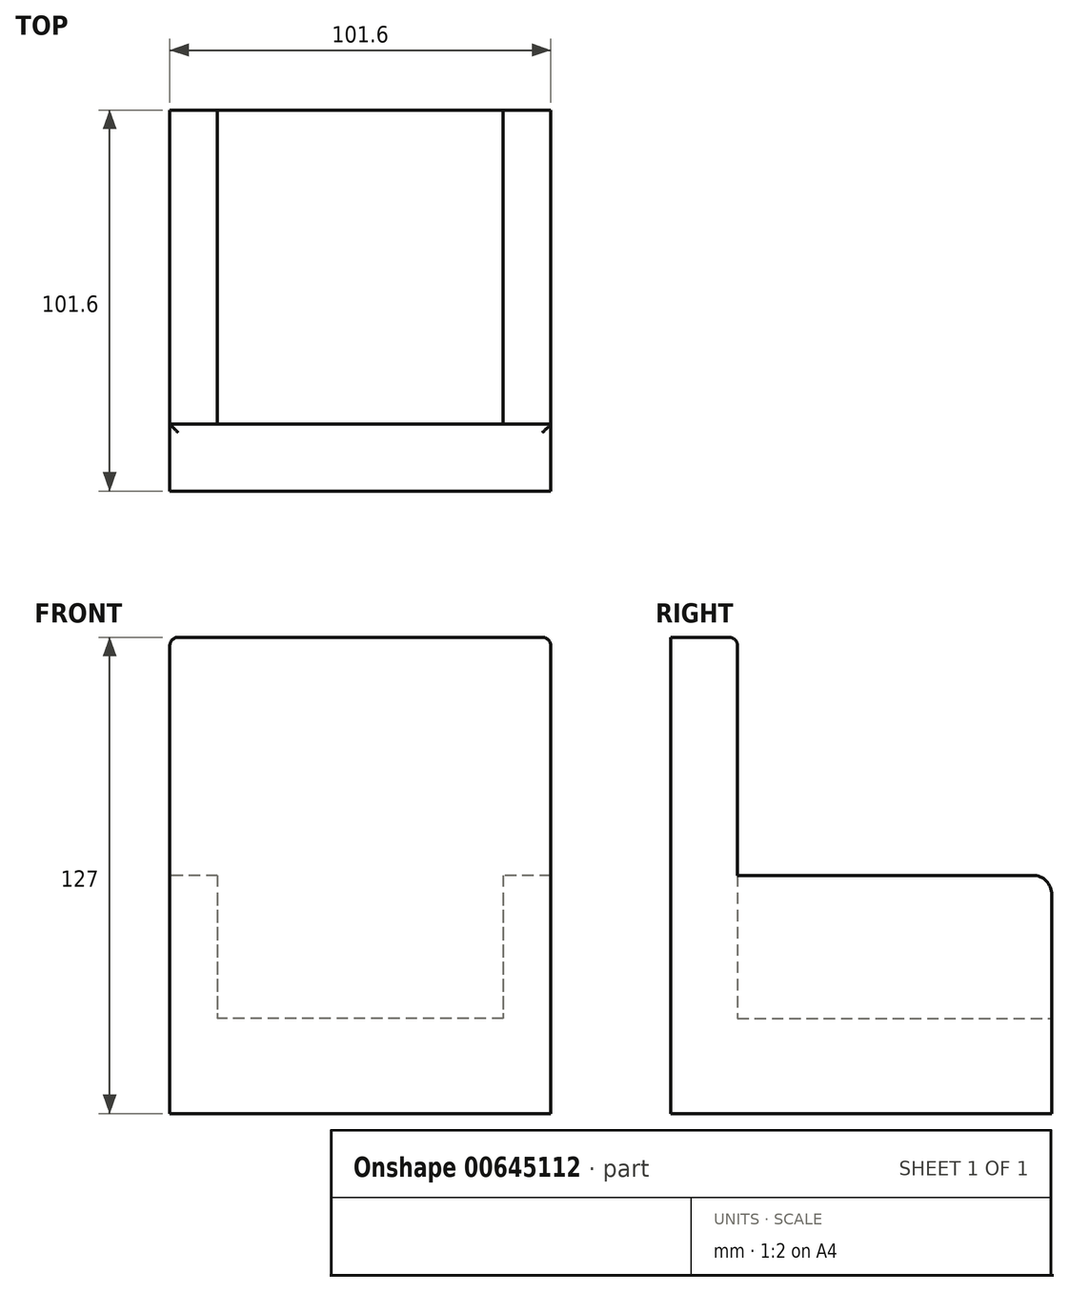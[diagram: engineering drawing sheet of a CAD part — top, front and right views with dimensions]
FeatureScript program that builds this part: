
annotation { "Feature Type Name" : "Feature", "Feature Type Description" : "" }
export const myFeature = defineFeature(function(context is Context, id is Id, definition is map)
    precondition{}
    {
        {
            var Q0;
            Q0=qCreatedBy(makeId("Top.planeOp"),FACE);
            var sketch = newSketch(context, id + "F0", { "sketchPlane" : qUnion([Q0])});
            skLineSegment(sketch, "E0.bottom", {"start": v(-50.64, 54.03) * mm, "end": v(50.96, 54.03) * mm});
            skLineSegment(sketch, "E0.top", {"start": v(-50.64, -47.57) * mm, "end": v(50.96, -47.57) * mm});
            skLineSegment(sketch, "E0.left", {"start": v(-50.64, 54.03) * mm, "end": v(-50.64, -47.57) * mm});
            skLineSegment(sketch, "E0.right", {"start": v(50.96, 54.03) * mm, "end": v(50.96, -47.57) * mm});
            skSolve(sketch);
        }
        {
            var Q0;
            Q0 = qSketchRegion(id + "F0", true);
            extrude(context, id + "F1", {"entities" : qUnion([Q0]), "depth" : 25.4 * mm, "offsetDistance" : 25.4 * mm});
        }
        {
            var Q0;
            Q0=makeQuery(id+"F1.opExtrude","CAP_FACE",FACE,{"disambiguationData":[OSD([sQuery(id+"F0.wireOp",EDGE,"E0.bottom"),sQuery(id+"F0.wireOp",EDGE,"E0.top"),sQuery(id+"F0.wireOp",EDGE,"E0.left"),sQuery(id+"F0.wireOp",EDGE,"E0.right")])],"isStart":false});
            var sketch = newSketch(context, id + "F2", { "sketchPlane" : qUnion([Q0])});
            skLineSegment(sketch, "E1.bottom", {"start": v(50.96, -47.57) * mm, "end": v(-50.64, -47.57) * mm});
            skLineSegment(sketch, "E1.top", {"start": v(50.96, -29.78) * mm, "end": v(-50.64, -29.78) * mm});
            skLineSegment(sketch, "E1.left", {"start": v(50.96, -47.57) * mm, "end": v(50.96, -29.78) * mm});
            skLineSegment(sketch, "E1.right", {"start": v(-50.64, -47.57) * mm, "end": v(-50.64, -29.78) * mm});
            skSolve(sketch);
        }
        {
            var Q0;
            Q0 = qSketchRegion(id + "F2", true);
            extrude(context, id + "F3", {"entities" : qUnion([Q0]), "operationType" : NewBodyOperationType.ADD, "depth" : 101.6 * mm, "offsetDistance" : 25.4 * mm});
        }
        {
            var Q0;
            Q0=makeQuery(id+"F1.opExtrude","CAP_FACE",FACE,{"disambiguationData":[OSD([sQuery(id+"F0.wireOp",EDGE,"E0.bottom"),sQuery(id+"F0.wireOp",EDGE,"E0.top"),sQuery(id+"F0.wireOp",EDGE,"E0.left"),sQuery(id+"F0.wireOp",EDGE,"E0.right")])],"isStart":false});
            var sketch = newSketch(context, id + "F4", { "sketchPlane" : qUnion([Q0])});
            skLineSegment(sketch, "E2.bottom", {"start": v(50.96, -29.78) * mm, "end": v(38.26, -29.78) * mm});
            skLineSegment(sketch, "E2.top", {"start": v(50.96, 54.03) * mm, "end": v(38.26, 54.03) * mm});
            skLineSegment(sketch, "E2.left", {"start": v(50.96, -29.78) * mm, "end": v(50.96, 54.03) * mm});
            skLineSegment(sketch, "E2.right", {"start": v(38.26, -29.78) * mm, "end": v(38.26, 54.03) * mm});
            skLineSegment(sketch, "E3.bottom", {"start": v(-50.64, -29.78) * mm, "end": v(-37.94, -29.78) * mm});
            skLineSegment(sketch, "E3.top", {"start": v(-50.64, 54.03) * mm, "end": v(-37.94, 54.03) * mm});
            skLineSegment(sketch, "E3.left", {"start": v(-50.64, -29.78) * mm, "end": v(-50.64, 54.03) * mm});
            skLineSegment(sketch, "E3.right", {"start": v(-37.94, -29.78) * mm, "end": v(-37.94, 54.03) * mm});
            skSolve(sketch);
        }
        {
            var Q0;
            Q0=makeQuery(id+"F4.imprint","IMPRINT",FACE,{"disambiguationData":[TD([[makeQuery(id+"F4.imprint","IMPRINT",EDGE,{"derivedFrom":sQuery(id+"F4.wireOp",EDGE,"E2.bottom")}),-1.0]])]});
            var Q1;
            Q1=makeQuery(id+"F4.imprint","IMPRINT",FACE,{"disambiguationData":[TD([[makeQuery(id+"F4.imprint","IMPRINT",EDGE,{"derivedFrom":sQuery(id+"F4.wireOp",EDGE,"E3.bottom")}),-1.0]])]});
            extrude(context, id + "F5", {"entities" : qUnion([Q0, Q1]), "operationType" : NewBodyOperationType.ADD, "depth" : 38.1 * mm, "offsetDistance" : 25.4 * mm});
        }
        {
            var Q0;
            Q0=makeQuery(id+"F5.opExtrude","CAP_EDGE",EDGE,{"disambiguationData":[OSD([sQuery(id+"F4.wireOp",EDGE,"E2.top")])],"isStart":false});
            fillet(context, id + "F6", {"entities" : qUnion([Q0]), "radius" : 5.08 * mm, "tangentPropagation" : true, "allowEdgeOverflow" : false});
        }
        {
            var Q0;
            Q0=makeQuery(id+"F5.opExtrude","CAP_EDGE",EDGE,{"disambiguationData":[OSD([sQuery(id+"F4.wireOp",EDGE,"E3.top")])],"isStart":false});
            fillet(context, id + "F7", {"entities" : qUnion([Q0]), "radius" : 5.08 * mm, "tangentPropagation" : true, "allowEdgeOverflow" : false});
        }
        {
            var Q0;
            Q0=makeQuery(id+"F3.opExtrude","CAP_EDGE",EDGE,{"disambiguationData":[OSD([sQuery(id+"F2.wireOp",EDGE,"E1.top")])],"isStart":false});
            var Q1;
            Q1=makeQuery(id+"F3.opExtrude","CAP_EDGE",EDGE,{"disambiguationData":[OSD([sQuery(id+"F2.wireOp",EDGE,"E1.right")])],"isStart":false});
            var Q2;
            Q2=makeQuery(id+"F3.opExtrude","CAP_EDGE",EDGE,{"disambiguationData":[OSD([sQuery(id+"F2.wireOp",EDGE,"E1.left")])],"isStart":false});
            fillet(context, id + "F8", {"entities" : qUnion([Q0, Q1, Q2]), "radius" : 2.3 * mm, "tangentPropagation" : true, "allowEdgeOverflow" : false});
        }
    });
